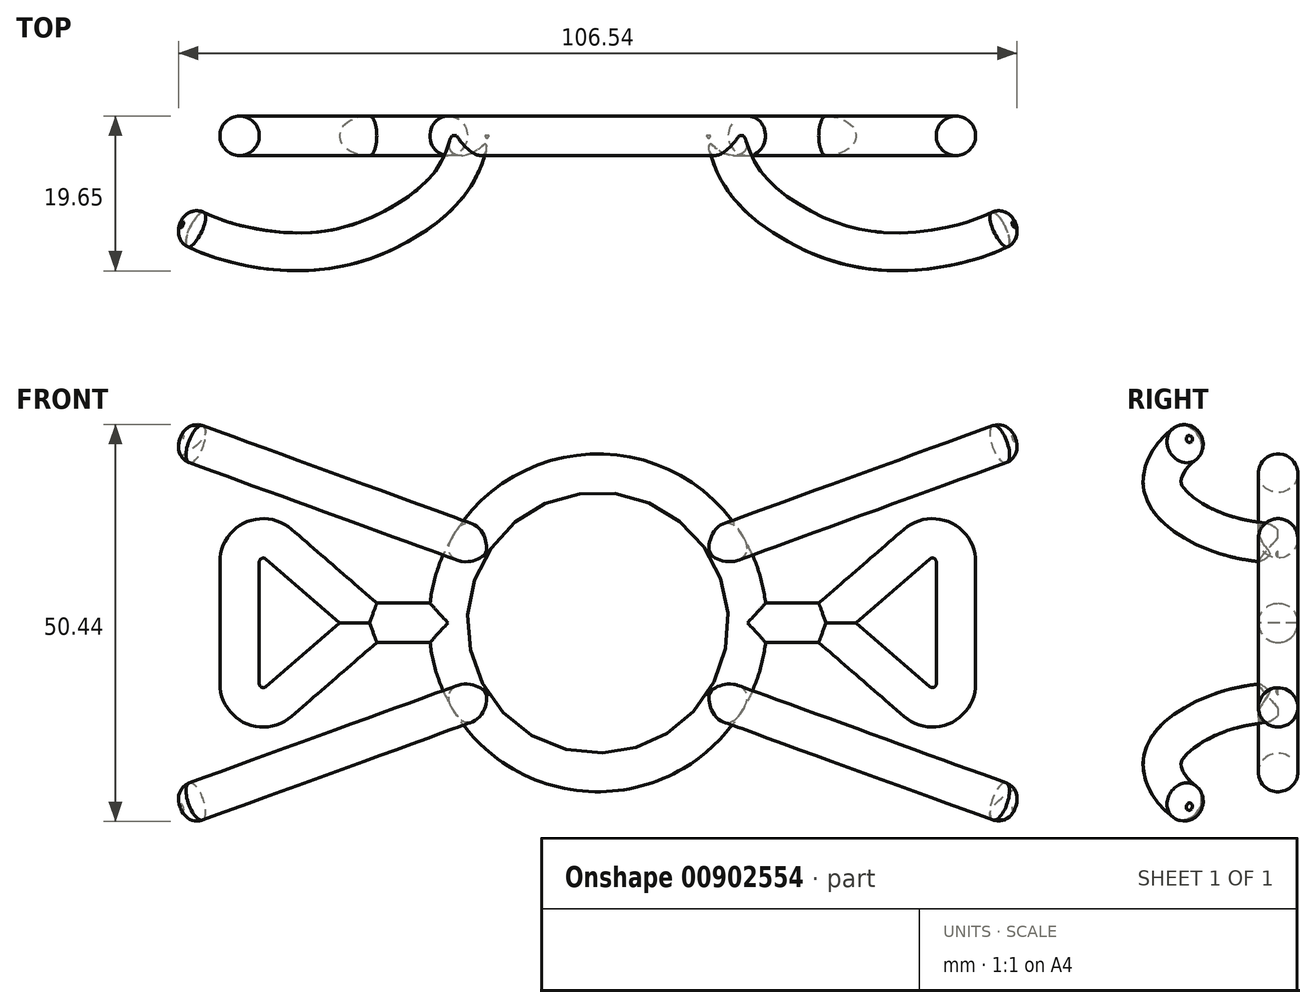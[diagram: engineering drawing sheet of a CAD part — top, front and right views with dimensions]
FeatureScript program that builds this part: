
annotation { "Feature Type Name" : "Feature", "Feature Type Description" : "" }
export const myFeature = defineFeature(function(context is Context, id is Id, definition is map)
    precondition{}
    {
        {
            var Q0;
            Q0=qCreatedBy(makeId("Front.planeOp"),FACE);
            var sketch = newSketch(context, id + "F0", { "sketchPlane" : qUnion([Q0])});
            skCircle(sketch, "E0", {"center": v(0, 0) * mm, "radius": 19 * mm});
            skLineSegment(sketch, "E1", {"start": v(16.16, 10) * mm, "end": v(51.86, 23) * mm});
            skCircle(sketch, "E2", {"center": v(16.16, 10) * mm, "radius": 2.5 * mm});
            skLineSegment(sketch, "E3", {"start": v(19, 0) * mm, "end": v(45.5, 0) * mm, "construction": true});
            skPoint(sketch, "E4", {"position": v(29, 0) * mm});
            skLineSegment(sketch, "E5", {"start": v(19, 0) * mm, "end": v(29, 0) * mm});
            skLineSegment(sketch, "E6", {"start": v(29, 0) * mm, "end": v(40.53, 10) * mm});
            skLineSegment(sketch, "E7", {"start": v(45.5, 7.74) * mm, "end": v(45.5, -7.74) * mm});
            skLineSegment(sketch, "E8", {"start": v(40.53, -10) * mm, "end": v(29, 0) * mm});
            skPoint(sketch, "E9.visualSharp", {"position": v(45.5, 14.3) * mm});
            skArc(sketch, "E9.filletArc", {"start": v(45.5, 7.74) * mm, "mid": v(43.75, 10.47) * mm, "end": v(40.53, 10) * mm});
            skPoint(sketch, "E10.visualSharp", {"position": v(45.5, -14.3) * mm});
            skArc(sketch, "E10.filletArc", {"start": v(40.53, -10) * mm, "mid": v(43.75, -10.47) * mm, "end": v(45.5, -7.74) * mm});
            skSolve(sketch);
        }
        {
            var Q0;
            Q0=sQuery(id+"F0.wireOp",EDGE,"E1");
            cPlane(context, id + "F1", {"entities" : qUnion([Q0]), "cplaneType" : CPlaneType.LINE_ANGLE, "offset" : 25 * mm, "angle" : 90 * degree, "width" : 150 * mm, "height" : 150 * mm});
        }
        {
            var Q0;
            Q0=qCreatedBy(id+"F1.planeOp",FACE);
            var sketch = newSketch(context, id + "F2", { "sketchPlane" : qUnion([Q0])});
            skFitSpline(sketch, "E11", {"points": [v(18.6, 0) * mm, v(22.61, -7.3) * mm, v(38.9, -14.58) * mm, v(57.52, -10.9) * mm], "startDerivative": vector(10.2, -36.34) * mm, "endDerivative": vector(26.66, 18) * mm});
            skCircle(sketch, "E12", {"center": v(18.6, 0) * mm, "radius": 2.5 * mm});
            skSolve(sketch);
        }
        {
            var Q0;
            {var subQ0=sQuery(id+"F0.wireOp",EDGE,"E0");var subQ1=makeQuery(id+"F0.imprint","INTERSECT",VERTEX,{"derivedFrom":[subQ0,sQuery(id+"F0.wireOp",EDGE,"E1")]});Q0=makeQuery(id+"F0.imprint","IMPRINT",FACE,{"disambiguationData":[TD([[makeQuery(id+"F0.imprint","IMPRINT",EDGE,{"disambiguationData":[TD([[subQ1,1.0]])],"derivedFrom":subQ0}),1.0]])]});}
            var Q1;
            {var subQ0=sQuery(id+"F0.wireOp",EDGE,"E1");var subQ1=sQuery(id+"F0.wireOp",EDGE,"E0");var subQ2=makeQuery(id+"F0.imprint","INTERSECT",VERTEX,{"derivedFrom":[subQ1,subQ0]});Q1=makeQuery(id+"F0.imprint","IMPRINT",FACE,{"disambiguationData":[TD([[makeQuery(id+"F0.imprint","IMPRINT",EDGE,{"disambiguationData":[TD([[subQ2,-1.0]])],"derivedFrom":subQ1}),-1.0]])]});}
            var Q2;
            {var subQ0=sQuery(id+"F0.wireOp",EDGE,"E1");var subQ1=sQuery(id+"F0.wireOp",EDGE,"E0");var subQ2=makeQuery(id+"F0.imprint","INTERSECT",VERTEX,{"derivedFrom":[subQ1,subQ0]});Q2=makeQuery(id+"F0.imprint","IMPRINT",FACE,{"disambiguationData":[TD([[makeQuery(id+"F0.imprint","IMPRINT",EDGE,{"disambiguationData":[TD([[subQ2,1.0]])],"derivedFrom":subQ1}),-1.0]])]});}
            var Q3;
            Q3=sQuery(id+"F2.wireOp",EDGE,"E11");
            sweep(context, id + "F3", {"profiles" : qUnion([Q0, Q1, Q2]), "path" : qUnion([Q3])});
        }
        {
            var Q0;
            Q0=makeQuery(id+"F3.opSweep","SWEPT_BODY",BODY,{"disambiguationData":[OSD([sQuery(id+"F0.wireOp",EDGE,"E2"),sQuery(id+"F2.wireOp",EDGE,"E11")])]});
            var Q1;
            Q1=qCreatedBy(makeId("Right.planeOp"),FACE);
            mirror(context, id + "F4", {"entities" : qUnion([Q0]), "mirrorPlane" : qUnion([Q1])});
        }
        {
            var Q0;
            Q0=makeQuery(id+"F4.opPattern","COPY",BODY,{"derivedFrom":makeQuery(id+"F3.opSweep","SWEPT_BODY",BODY,{"disambiguationData":[OSD([sQuery(id+"F0.wireOp",EDGE,"E2"),sQuery(id+"F2.wireOp",EDGE,"E11")])]}),"instanceName":"1"});
            var Q1;
            Q1=makeQuery(id+"F3.opSweep","SWEPT_BODY",BODY,{"disambiguationData":[OSD([sQuery(id+"F0.wireOp",EDGE,"E2"),sQuery(id+"F2.wireOp",EDGE,"E11")])]});
            var Q2;
            Q2=qCreatedBy(makeId("Top.planeOp"),FACE);
            mirror(context, id + "F5", {"entities" : qUnion([Q0, Q1]), "mirrorPlane" : qUnion([Q2])});
        }
        {
            var Q0;
            Q0=makeQuery(id+"F3.opSweep","CAP_EDGE",EDGE,{"disambiguationData":[OSD([sQuery(id+"F0.wireOp",EDGE,"E2"),sQuery(id+"F2.wireOp",VERTEX,"E11.end")])],"isStart":false});
            var Q1;
            Q1=makeQuery(id+"F5.opPattern","COPY",EDGE,{"derivedFrom":makeQuery(id+"F3.opSweep","CAP_EDGE",EDGE,{"disambiguationData":[OSD([sQuery(id+"F0.wireOp",EDGE,"E2"),sQuery(id+"F2.wireOp",VERTEX,"E11.end")])],"isStart":false}),"instanceName":"1"});
            var Q2;
            Q2=makeQuery(id+"F5.opPattern","COPY",EDGE,{"derivedFrom":makeQuery(id+"F4.opPattern","COPY",EDGE,{"derivedFrom":makeQuery(id+"F3.opSweep","CAP_EDGE",EDGE,{"disambiguationData":[OSD([sQuery(id+"F0.wireOp",EDGE,"E2"),sQuery(id+"F2.wireOp",VERTEX,"E11.end")])],"isStart":false}),"instanceName":"1"}),"instanceName":"1"});
            var Q3;
            Q3=makeQuery(id+"F4.opPattern","COPY",EDGE,{"derivedFrom":makeQuery(id+"F3.opSweep","CAP_EDGE",EDGE,{"disambiguationData":[OSD([sQuery(id+"F0.wireOp",EDGE,"E2"),sQuery(id+"F2.wireOp",VERTEX,"E11.end")])],"isStart":false}),"instanceName":"1"});
            fillet(context, id + "F6", {"entities" : qUnion([Q0, Q1, Q2, Q3]), "radius" : 2 * mm, "allowEdgeOverflow" : false});
        }
        {
            var Q0;
            Q0=qCreatedBy(makeId("Top.planeOp"),FACE);
            var sketch = newSketch(context, id + "F7", { "sketchPlane" : qUnion([Q0])});
            skCircle(sketch, "E13", {"center": v(45.5, 0) * mm, "radius": 2.5 * mm});
            skSolve(sketch);
        }
        {
            var Q0;
            Q0=sQuery(id+"F0.wireOp",VERTEX,"E3.start");
            var Q1;
            Q1=qCreatedBy(makeId("Right.planeOp"),FACE);
            cPlane(context, id + "F8", {"entities" : qUnion([Q0, Q1]), "cplaneType" : CPlaneType.PLANE_POINT, "offset" : 25 * mm, "width" : 150 * mm, "height" : 150 * mm});
        }
        {
            var Q0;
            Q0=qCreatedBy(id+"F8.planeOp",FACE);
            var sketch = newSketch(context, id + "F9", { "sketchPlane" : qUnion([Q0])});
            skCircle(sketch, "E14", {"center": v(0, 0) * mm, "radius": 2.5 * mm});
            skSolve(sketch);
        }
        {
            var Q0;
            Q0=makeQuery(id+"F7.imprint","IMPRINT",FACE,{"disambiguationData":[TD([[makeQuery(id+"F7.imprint","IMPRINT",EDGE,{"derivedFrom":sQuery(id+"F7.wireOp",EDGE,"E13")}),1.0]])]});
            var Q1;
            Q1=sQuery(id+"F0.wireOp",EDGE,"E7");
            var Q2;
            Q2=sQuery(id+"F0.wireOp",EDGE,"E9.filletArc");
            var Q3;
            Q3=sQuery(id+"F0.wireOp",EDGE,"E6");
            var Q4;
            Q4=sQuery(id+"F0.wireOp",EDGE,"E8");
            var Q5;
            Q5=sQuery(id+"F0.wireOp",EDGE,"E10.filletArc");
            sweep(context, id + "F10", {"operationType" : NewBodyOperationType.ADD, "profiles" : qUnion([Q0]), "path" : qUnion([Q1, Q2, Q3, Q4, Q5])});
        }
        {
            var Q0;
            Q0 = qSketchRegion(id + "F9", true);
            var Q1;
            Q1=sQuery(id+"F0.wireOp",EDGE,"E5");
            sweep(context, id + "F11", {"operationType" : NewBodyOperationType.ADD, "profiles" : qUnion([Q0]), "path" : qUnion([Q1])});
        }
        {
            var Q0;
            Q0=makeQuery(id+"F10.opSweep","SWEPT_BODY",BODY,{"disambiguationData":[OSD([sQuery(id+"F0.wireOp",EDGE,"E9.filletArc"),sQuery(id+"F7.wireOp",EDGE,"E13")])]});
            var Q1;
            Q1=qCreatedBy(makeId("Right.planeOp"),FACE);
            mirror(context, id + "F12", {"entities" : qUnion([Q0]), "mirrorPlane" : qUnion([Q1])});
        }
        {
            var Q0;
            Q0=makeQuery(id+"F2.imprint","IMPRINT",FACE,{"disambiguationData":[TD([[makeQuery(id+"F2.imprint","IMPRINT",EDGE,{"derivedFrom":sQuery(id+"F2.wireOp",EDGE,"E12")}),1.0]])]});
            var Q1;
            Q1=sQuery(id+"F0.wireOp",EDGE,"E0");
            sweep(context, id + "F13", {"operationType" : NewBodyOperationType.ADD, "profiles" : qUnion([Q0]), "path" : qUnion([Q1])});
        }
    });
